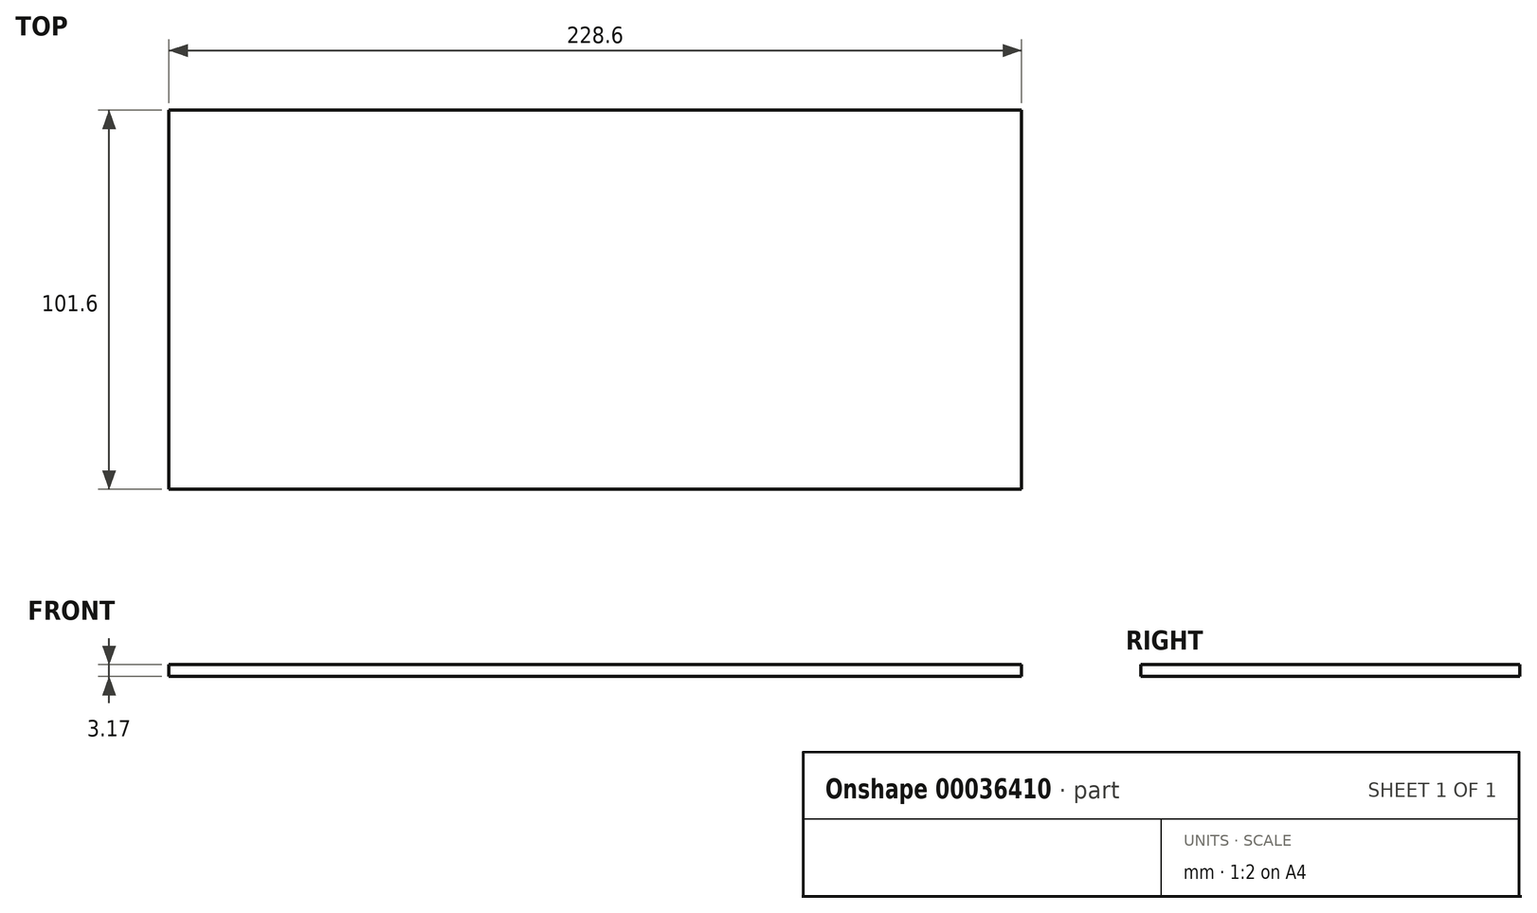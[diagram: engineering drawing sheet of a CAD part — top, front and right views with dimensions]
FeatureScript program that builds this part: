
annotation { "Feature Type Name" : "Feature", "Feature Type Description" : "" }
export const myFeature = defineFeature(function(context is Context, id is Id, definition is map)
    precondition{}
    {
        {
            var Q0;
            Q0=qCreatedBy(makeId("Top.planeOp"),FACE);
            var sketch = newSketch(context, id + "F0", { "sketchPlane" : qUnion([Q0])});
            skLineSegment(sketch, "E0.rect.bottom", {"start": v(114.3, 50.8) * mm, "end": v(-114.3, 50.8) * mm});
            skLineSegment(sketch, "E0.rect.top", {"start": v(114.3, -50.8) * mm, "end": v(-114.3, -50.8) * mm});
            skLineSegment(sketch, "E0.rect.left", {"start": v(114.3, 50.8) * mm, "end": v(114.3, -50.8) * mm});
            skLineSegment(sketch, "E0.rect.right", {"start": v(-114.3, 50.8) * mm, "end": v(-114.3, -50.8) * mm});
            skPoint(sketch, "E0.rect.middle", {"position": v(0, 0) * mm});
            skSolve(sketch);
        }
        {
            var Q0;
            Q0=makeQuery(id+"F0.imprint","IMPRINT",FACE,{"disambiguationData":[TD([[makeQuery(id+"F0.imprint","IMPRINT",EDGE,{"derivedFrom":sQuery(id+"F0.wireOp",EDGE,"E0.rect.bottom")}),1.0]])]});
            extrude(context, id + "F1", {"entities" : qUnion([Q0]), "depth" : 3.17 * mm});
        }
    });
